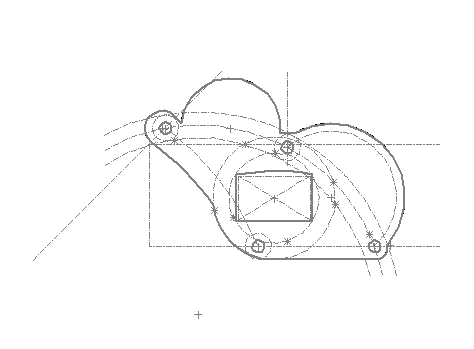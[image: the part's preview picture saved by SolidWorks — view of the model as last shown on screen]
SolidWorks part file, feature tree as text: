
SOLIDWORKS PART (.sldprt)
format: sldprt  version: not decoded by parser v0  size: 704,512 bytes
history: native  units: mm
features: extrude x64, sketch x6, plane x1 (+10 scaffold rows collapsed)
feature tree (81):
  scaffold x10  (default folders/planes/origin — collapsed)
  sketch  "Sketch1"  dims[c1.D7=10.3124mm c1.D8=10.3124mm c1.D9=10.3124mm c1.D10=10.3124mm c1.D14=10.3124mm c1.D18=28.448mm c1.D19=28.448mm c1.D20=28.448mm c1.D21=28.448mm c1.D22=28.448mm c2.D18=14.224mm c2.D21=14.224mm c2.D19=22.86mm c2.D20=28.448mm c3.D21=22.86mm c3.D18=28.448mm c3.D22=~37.026545mm c3.D20=22.86mm c4.D22=22.86mm c4.D23=~312.928058mm c4.D16=78.74mm c4.D18=~312.928058mm c5.D16=78.74mm c5.D18=78.74mm c5.D23=55.88mm c5.D1=10.3124mm c5.D2=10.3124mm c5.D3=10.3124mm c5.D4=10.3124mm c5.D5=22.86mm c5.D6=22.86mm c5.D7=22.86mm c5.D8=22.86mm c6.D4=10.3124mm c6.D5=22.86mm c6.D18=10.3124mm c6.D10=10.3124mm c6.D16=22.86mm c6.D25=78.74mm c6.D26=107.188mm c6.D27=2.54mm c6.D28=2.54mm c6.D29=53.594mm c7.D28=53.594mm c7.D27=~7.860749mm c7.D5=2.54mm c7.D1=196.85mm c7.D2=88.9mm c7.D3=77.47mm c7.D4=22.86mm c8.D5=63.5mm c8.D6=38.1mm c8.D11=95.25mm c8.D12=120.65mm c8.D13=12.7mm c8.D14=12.7mm c9.D14=~47.123606deg c10.D14=12.7mm c11.D14=45.0deg c11.D15=12.7mm c11.D16=12.7mm c11.D13=12.7mm c11.D17=12.7mm c11.D19=101.6mm c11.D20=14.224mm c11.D18=14.224mm c11.D22=101.6mm c12.D18=12.7mm c12.D13=~70.473173mm c13.D13=45.0deg c13.D14=20.32mm c13.D23=12.7mm c13.D24=12.7mm c13.D17=12.7mm c13.D18=12.7mm c13.D9=88.9mm c13.D10=120.65mm c13.D11=196.85mm c13.D12=95.25mm c14.D13=77.47mm c14.D12=63.5mm c14.D14=22.86mm c14.D15=38.1mm c14.D16=20.32mm c14.D17=120.65mm c15.D17=45.0deg c15.D11=95.25mm c15.D18=196.85mm c15.D10=120.65mm c15.D16=12.7mm c15.D19=12.7mm c16.D16=12.7mm c16.D19=~19.235521mm c16.D7=120.65mm c16.D10=12.7mm c17.D10=90.0deg c17.D19=12.7mm c17.D20=12.7mm c17.D21=12.7mm c17.D22=12.7mm c17.D23=2.54mm c17.D24=20.32mm c17.D25=63.5mm c18.D23=2.54mm c18.D18=~175.82368deg c18.D16=~174.212182deg]
  extrude  "Extrude1"  Depth=6.35mm cosMaterialEX=10009317
  extrude  "sMaterialName"  [1 undecoded]
  extrude  "cosFMVItemName"  [1 undecoded]
  extrude  "cosMaterialName"  [1 undecoded]
  extrude  "cosComponentName"  [1 undecoded]
  extrude  "cosMaterialType"  [1 undecoded]
  extrude  "cosMaterialLibFile"  [1 undecoded]
  extrude  "cosMaterialRefPlaneName"  [1 undecoded]
  extrude  "sMaterialSourceName"  [1 undecoded]
  extrude  "sMaterialName"  [1 undecoded]
  extrude  "cosFMVItemName"  [1 undecoded]
  extrude  "cosMaterialName"  [1 undecoded]
  extrude  "cosComponentName"  [1 undecoded]
  extrude  "cosMaterialType"  [1 undecoded]
  extrude  "cosMaterialLibFile"  [1 undecoded]
  extrude  "cosMaterialRefPlaneName"  [1 undecoded]
  extrude  "cosRestraintRefPlaneName"  [1 undecoded]
  extrude  "cosFMVItemName"  [1 undecoded]
  extrude  "cosLBCSymbolColor"  Depth=0 cosRestraint7=0
  extrude  "cosRestraintRefPlaneName"  [1 undecoded]
  extrude  "cosFMVItemName"  [1 undecoded]
  extrude  "cosLBCSymbolColor"  [1 undecoded]
  extrude  "cosRestraintRefPlaneName"  [1 undecoded]
  extrude  "cosFMVItemName"  [1 undecoded]
  extrude  "cosLBCSymbolColor"  [1 undecoded]
  extrude  "cosForceRefPlaneName"  [1 undecoded]
  extrude  "cosFMVItemName"  [1 undecoded]
  extrude  "cosDistributionCoordSysName"  [1 undecoded]
  extrude  "cosLBCSymbolColor"  Depth=0 cosForce7=0
  extrude  "cosForceRefPlaneName"  [1 undecoded]
  extrude  "cosFMVItemName"  [1 undecoded]
  extrude  "cosDistributionCoordSysName"  [1 undecoded]
  extrude  "cosLBCSymbolColor"  [1 undecoded]
  extrude  "cosForceRefPlaneName"  [1 undecoded]
  extrude  "cosFMVItemName"  [1 undecoded]
  extrude  "cosDistributionCoordSysName"  [1 undecoded]
  extrude  "cosLBCSymbolColor"  [1 undecoded]
  extrude  "Extrude4"  [1 undecoded]
  sketch  "Sketch1<11>"  dims[D1=6.35mm]
  extrude  "Extrude5"  [1 undecoded]
  sketch  "Sketch1<12>"  dims[D1=6.35mm]
  plane  "Plane1"
  extrude  "Extrude6"  [1 undecoded]
  sketch  "Sketch1<13>"  dims[D1=6.35mm]
  extrude  "Extrude7"  [1 undecoded]
  sketch  "Sketch1<14>"  dims[D1=6.35mm]
  extrude  "Extrude8"  [1 undecoded]
  sketch  "Sketch1<15>"  dims[D1=6.35mm]
  extrude  "sMaterialSourceName"  [1 undecoded]
  extrude  "sMaterialName"  [1 undecoded]
  extrude  "cosFMVItemName"  [1 undecoded]
  extrude  "cosMaterialName"  [1 undecoded]
  extrude  "cosComponentName"  [1 undecoded]
  extrude  "cosMaterialType"  [1 undecoded]
  extrude  "cosMaterialLibFile"  [1 undecoded]
  extrude  "cosMaterialRefPlaneName"  [1 undecoded]
  extrude  "cosRestraintRefPlaneName"  [1 undecoded]
  extrude  "cosFMVItemName"  [1 undecoded]
  extrude  "cosLBCSymbolColor"  [1 undecoded]
  extrude  "cosRestraintRefPlaneName"  [1 undecoded]
  extrude  "cosFMVItemName"  [1 undecoded]
  extrude  "cosLBCSymbolColor"  [1 undecoded]
  extrude  "cosForceRefPlaneName"  [1 undecoded]
  extrude  "cosFMVItemName"  [1 undecoded]
  extrude  "cosDistributionCoordSysName"  [1 undecoded]
  extrude  "cosLBCSymbolColor"  [1 undecoded]
  extrude  "cosForceRefPlaneName"  [1 undecoded]
  extrude  "cosFMVItemName"  [1 undecoded]
  extrude  "cosDistributionCoordSysName"  [1 undecoded]
  extrude  "cosLBCSymbolColor"  Depth=0 cosFaceID=0
decode coverage: 10 of 70 modeling features carry decoded parameters
note: ~ marks probable driven/reference dimensions
note: 60 parameter values undecoded
summary: no parameter record found for 60 features
note: suppression state not decoded; provenance and decode notes live in map.json
